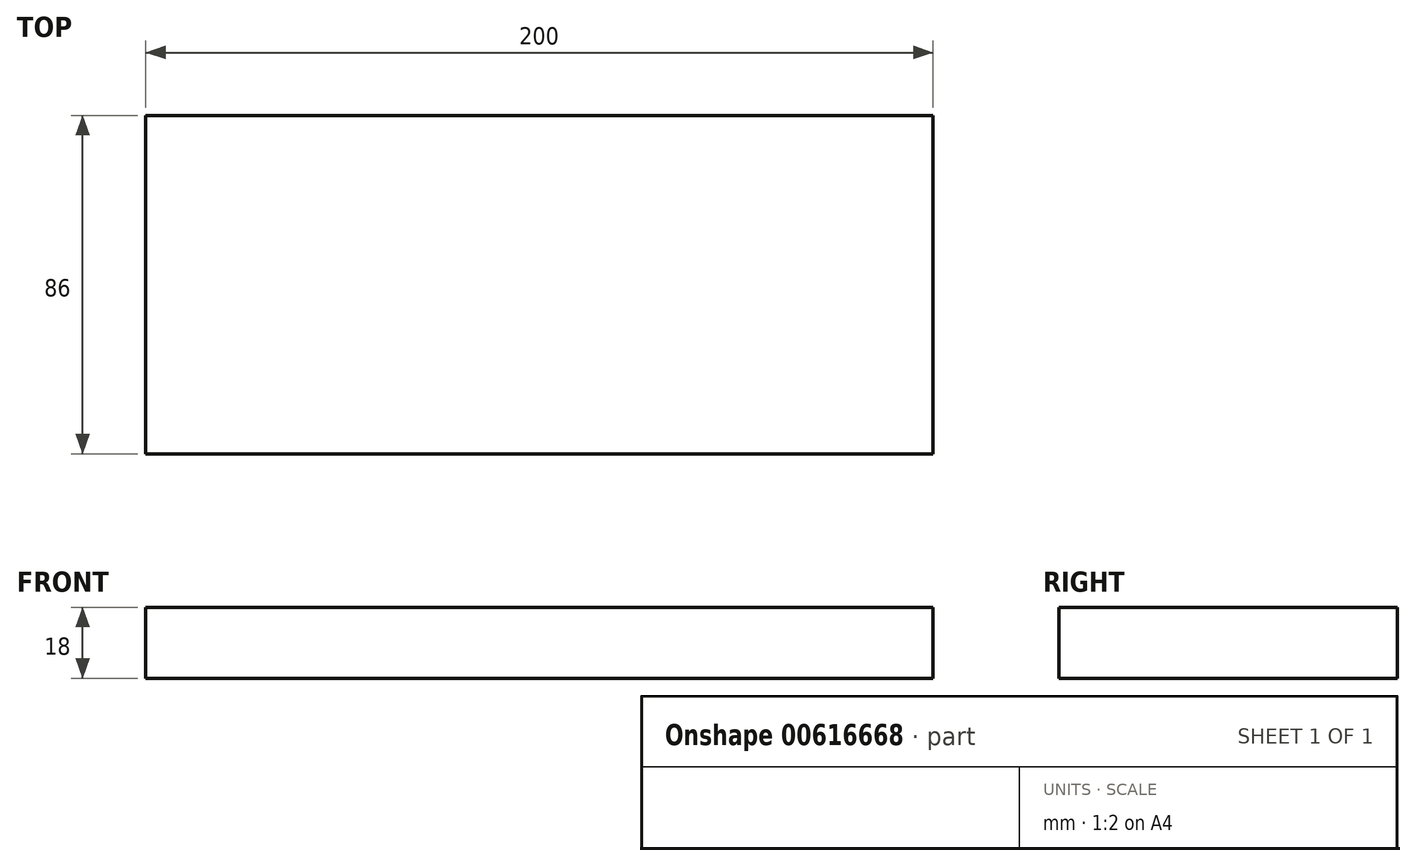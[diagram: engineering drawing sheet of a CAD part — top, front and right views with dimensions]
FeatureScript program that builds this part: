
annotation { "Feature Type Name" : "Feature", "Feature Type Description" : "" }
export const myFeature = defineFeature(function(context is Context, id is Id, definition is map)
    precondition{}
    {
        {
            var Q0;
            Q0=qCreatedBy(makeId("Top.planeOp"),FACE);
            var sketch = newSketch(context, id + "F0", { "sketchPlane" : qUnion([Q0])});
            skLineSegment(sketch, "E0.bottom", {"start": v(0, 0) * mm, "end": v(200, 0) * mm});
            skLineSegment(sketch, "E0.top", {"start": v(0, 86) * mm, "end": v(200, 86) * mm});
            skLineSegment(sketch, "E0.left", {"start": v(0, 0) * mm, "end": v(0, 86) * mm});
            skLineSegment(sketch, "E0.right", {"start": v(200, 0) * mm, "end": v(200, 86) * mm});
            skSolve(sketch);
        }
        {
            var Q0;
            Q0=makeQuery(id+"F0.imprint","IMPRINT",FACE,{"disambiguationData":[TD([[makeQuery(id+"F0.imprint","IMPRINT",EDGE,{"derivedFrom":sQuery(id+"F0.wireOp",EDGE,"E0.bottom")}),1.0]])]});
            extrude(context, id + "F1", {"entities" : qUnion([Q0]), "depth" : 18 * mm, "offsetDistance" : 25 * mm});
        }
    });
